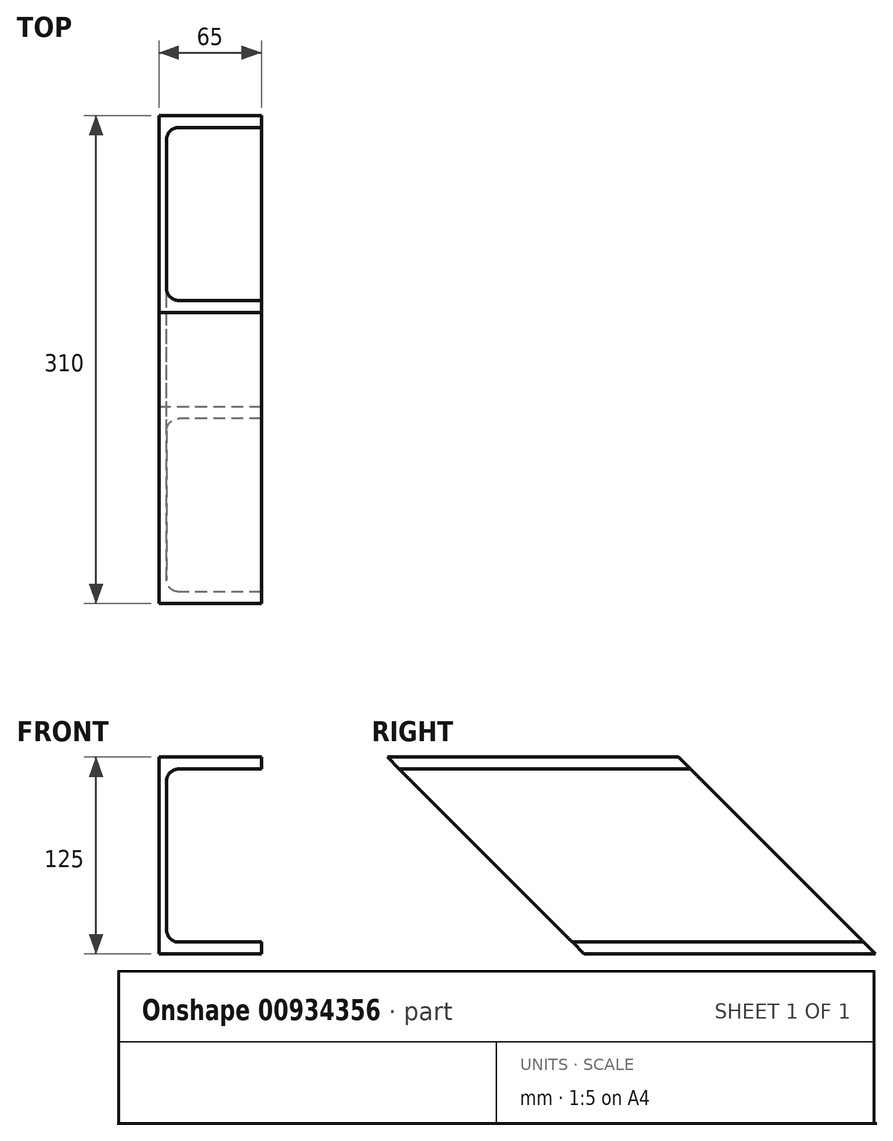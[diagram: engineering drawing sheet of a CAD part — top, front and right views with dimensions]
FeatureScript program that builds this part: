
annotation { "Feature Type Name" : "Feature", "Feature Type Description" : "" }
export const myFeature = defineFeature(function(context is Context, id is Id, definition is map)
    precondition{}
    {
        {
            var Q0;
            Q0=qCreatedBy(makeId("Front.planeOp"),FACE);
            var sketch = newSketch(context, id + "F0", { "sketchPlane" : qUnion([Q0])});
            skLineSegment(sketch, "E0", {"start": v(-25.17, -62.5) * mm, "end": v(-25.17, 62.5) * mm});
            skLineSegment(sketch, "E1", {"start": v(-25.17, 62.5) * mm, "end": v(39.83, 62.5) * mm});
            skLineSegment(sketch, "E2", {"start": v(39.83, 62.5) * mm, "end": v(39.83, 55) * mm});
            skLineSegment(sketch, "E3", {"start": v(39.83, 55) * mm, "end": v(-12.47, 55) * mm});
            skLineSegment(sketch, "E4", {"start": v(-25.17, -62.5) * mm, "end": v(39.83, -62.5) * mm});
            skLineSegment(sketch, "E5", {"start": v(39.83, -62.5) * mm, "end": v(39.83, -55) * mm});
            skLineSegment(sketch, "E6", {"start": v(39.83, -55) * mm, "end": v(-12.47, -55) * mm});
            skLineSegment(sketch, "E7", {"start": v(-20.47, -47) * mm, "end": v(-20.47, 47) * mm});
            skPoint(sketch, "E8.visualSharp", {"position": v(-20.47, 55) * mm});
            skArc(sketch, "E8.filletArc", {"start": v(-12.47, 55) * mm, "mid": v(-18.12, 52.66) * mm, "end": v(-20.47, 47) * mm});
            skPoint(sketch, "E9.visualSharp", {"position": v(-20.47, -55) * mm});
            skArc(sketch, "E9.filletArc", {"start": v(-20.47, -47) * mm, "mid": v(-18.12, -52.66) * mm, "end": v(-12.47, -55) * mm});
            skSolve(sketch);
        }
        {
            var Q0;
            Q0=makeQuery(id+"F0.imprint","IMPRINT",FACE,{"disambiguationData":[TD([[makeQuery(id+"F0.imprint","IMPRINT",EDGE,{"derivedFrom":sQuery(id+"F0.wireOp",EDGE,"E0")}),-1.0]])]});
            extrude(context, id + "F1", {"entities" : qUnion([Q0]), "depth" : 310 * mm, "offsetDistance" : 25 * mm});
        }
        {
            var Q0;
            Q0=makeQuery(id+"F1.opExtrude","SWEPT_FACE",FACE,{"disambiguationData":[OSD([sQuery(id+"F0.wireOp",EDGE,"E0")])]});
            var sketch = newSketch(context, id + "F2", { "sketchPlane" : qUnion([Q0])});
            skLineSegment(sketch, "E10", {"start": v(0, 62.5) * mm, "end": v(125, 62.5) * mm});
            skLineSegment(sketch, "E11", {"start": v(125, 62.5) * mm, "end": v(0, -62.5) * mm});
            skLineSegment(sketch, "E12", {"start": v(310, -62.5) * mm, "end": v(185, -62.5) * mm});
            skLineSegment(sketch, "E13", {"start": v(185, -62.5) * mm, "end": v(310, 62.5) * mm});
            skSolve(sketch);
        }
        {
            var Q0;
            Q0=makeQuery(id+"F2.imprint","IMPRINT",FACE,{"disambiguationData":[TD([[makeQuery(id+"F2.imprint","IMPRINT",EDGE,{"derivedFrom":sQuery(id+"F2.wireOp",EDGE,"E10")}),1.0]])]});
            var Q1;
            Q1=makeQuery(id+"F2.imprint","IMPRINT",FACE,{"disambiguationData":[TD([[makeQuery(id+"F2.imprint","IMPRINT",EDGE,{"derivedFrom":sQuery(id+"F2.wireOp",EDGE,"E12")}),-1.0]])]});
            extrude(context, id + "F3", {"entities" : qUnion([Q0, Q1]), "operationType" : NewBodyOperationType.REMOVE, "endBound" : BoundingType.THROUGH_ALL, "oppositeDirection" : true, "depth" : 25 * mm, "offsetDistance" : 25 * mm});
        }
    });
